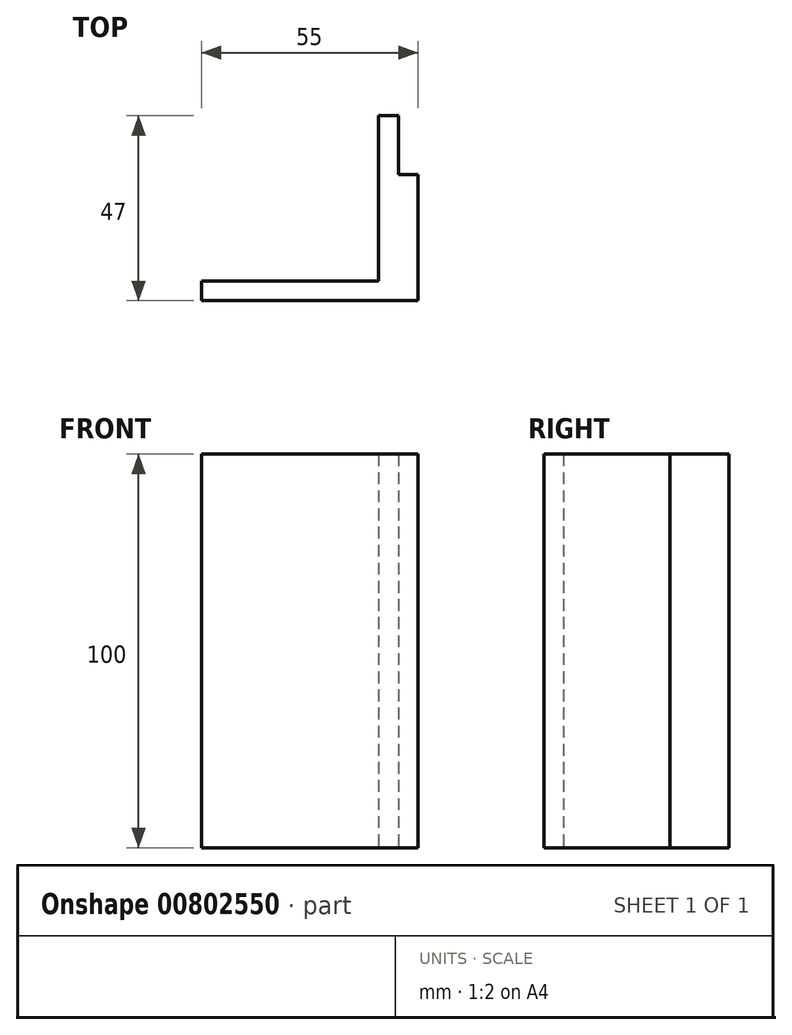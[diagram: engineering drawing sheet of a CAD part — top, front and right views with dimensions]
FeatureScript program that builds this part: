
annotation { "Feature Type Name" : "Feature", "Feature Type Description" : "" }
export const myFeature = defineFeature(function(context is Context, id is Id, definition is map)
    precondition{}
    {
        {
            var Q0;
            Q0=qCreatedBy(makeId("Top.planeOp"),FACE);
            var sketch = newSketch(context, id + "F0", { "sketchPlane" : qUnion([Q0])});
            skLineSegment(sketch, "E0.bottom", {"start": v(0, 0) * mm, "end": v(-5, 0) * mm});
            skLineSegment(sketch, "E0.top", {"start": v(0, 15) * mm, "end": v(-5, 15) * mm});
            skLineSegment(sketch, "E0.left", {"start": v(0, 0) * mm, "end": v(0, 15) * mm});
            skLineSegment(sketch, "E0.right", {"start": v(-5, 0) * mm, "end": v(-5, 15) * mm});
            skLineSegment(sketch, "E1.bottom", {"start": v(0, 0) * mm, "end": v(5, 0) * mm});
            skLineSegment(sketch, "E1.top", {"start": v(0, -5) * mm, "end": v(5, -5) * mm});
            skLineSegment(sketch, "E1.left", {"start": v(0, 0) * mm, "end": v(0, -5) * mm});
            skLineSegment(sketch, "E1.right", {"start": v(5, 0) * mm, "end": v(5, -5) * mm});
            skLineSegment(sketch, "E2.bottom", {"start": v(0, 0) * mm, "end": v(-50, 0) * mm});
            skLineSegment(sketch, "E2.top", {"start": v(0, -5) * mm, "end": v(-50, -5) * mm});
            skLineSegment(sketch, "E2.right", {"start": v(-50, 0) * mm, "end": v(-50, -5) * mm});
            skSolve(sketch);
        }
        {
            var Q0;
            Q0 = qSketchRegion(id + "F0", true);
            extrude(context, id + "F1", {"entities" : qUnion([Q0]), "depth" : 100 * mm, "offsetDistance" : 25.4 * mm});
        }
        {
            var Q0;
            Q0=makeQuery(id+"F1.opExtrude","SWEPT_FACE",FACE,{"disambiguationData":[OSD([sQuery(id+"F0.wireOp",EDGE,"E1.top"),sQuery(id+"F0.wireOp",EDGE,"E2.top")])]});
            extrude(context, id + "F2", {"entities" : qUnion([Q0]), "operationType" : NewBodyOperationType.ADD, "depth" : 27 * mm, "offsetDistance" : 25.4 * mm});
        }
        {
            var Q0;
            Q0=makeQuery(id+"F1.opExtrude","SWEPT_FACE",FACE,{"disambiguationData":[OSD([sQuery(id+"F0.wireOp",EDGE,"E2.bottom")])]});
            extrude(context, id + "F3", {"entities" : qUnion([Q0]), "operationType" : NewBodyOperationType.REMOVE, "oppositeDirection" : true, "depth" : 27 * mm, "offsetDistance" : 25.4 * mm});
        }
    });
